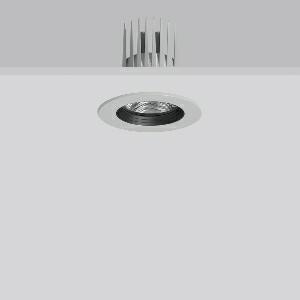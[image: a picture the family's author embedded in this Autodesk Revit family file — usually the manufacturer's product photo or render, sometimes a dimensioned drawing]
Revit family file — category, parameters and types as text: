
# Revit family: heledon_mini_e_901740_004_1_98e3
name_source: partatom
category: Lighting Fixtures
units: mm (PartAtom-declared; Revit-internal decimal feet)

## family parameters
Cut with Voids When Loaded = No
Host = Face
Light Source = No
Part Type = Normal
Room Calculation Point = No
Round Connector Dimension = Use Diameter
Shared = No

## types (1)
- HELEDON mini E (1 x LED Modul 940, 2700 lm, 4000)
    Apparent Load = 20 VA
    Approval mark = CE
    CIE Flux Codes = 100 100 100 100 100
    Color Rendering = 92
    Color Temperature = 4000
    Default Elevation = 1800 mm
    Description = Series: HELEDON mini
Round recessed downlight. Housing: die-cast aluminium, powder-coated. Black plastic ring and recessed LED to prevent glare from the side. Optical assembly with reflector made of MIRO-Silver with 98% total light reflection for outstanding efficiency - can be changed without tools. Best colour rendering index Ra>90. Suitable for Recessed ceiling mounting. Installation without tools thanks to spring fastening system. Including separate LED converter with connecting cable 600 mm.High quality converter without flickering and stroboscopic effect. Through-wiring box (5 pole) available as accessory. The following accessories can be mounted without use of tools: interchangeable lenses, decorative glasses, honeycomb louvre, clear and frosted diffusers, white interchangeable plastic ring. 
Colour: silver
Diameter: 124 mm
Height: 3 mm
Cut-out diameter: 114 mm
Recess height: 170 mm
Luminaire: recess height: 120 mm
Lamp: LED
Socket: without socket
Colour temperature: 4000K
Colour rendering index (CRI): 92
System power: 20 W
Rated luminous flux: 2700 lm
Luminous efficiency: 135 lm/W
Control gear: Regulated power supply
Protection class: II
Type of protection: IP 20
    Height = 0 mm  [stored 0 ft]
    Lamp = 1 x LED Modul 940
    Lamp Light Flux = 2700 lm
    Lamp count = 1
    Length = 124 mm  [stored 0.406824 ft]
    Lifetime = 50000 h
    Luminous efficacy = 135 lm/W
    Manufacturer = RZB
    ModVariant = No
    Model = 901740.004.1
    Mounting Place = Ceiling
    Mounting Type = Recessed
    Number of Poles = 1
    OnlyDefault = Yes
    Power Factor = 1
    Product Name = HELEDON mini E
    Product group = Recessed downlights
    ProductGroupID = 402
    Protection Class = Protection class II
    Protection Degree = IP 20
    RLX_Detail_Level = 1
    RLX_Emergency_Light_Flux = 0 lm
    RLX_Emergency_Type = 0
    RLX_Emergency_Type_DB = No
    RlxData = <blob elided: 127829 chars, md5=203a31c9>
    Socket = socket
    Standby Power = 0 W
    System Light Flux = 2700 lm
    System Power = 20 W
    Type Comments = Product without accessories
    Type Image = 901657.004.jpg
    URL = http://relux.com
    VarID = ---
    Voltage = 230 V
    Voltage Range = 220-240 V
    Weight = 0.00 kg
    Width = 0 mm  [stored 0 ft]

note: [stored X ft] marks values corroborated as IEEE doubles in the binary element streams (Revit-internal decimal feet)

## geometry (parser evidence)
native form markers: Blend x4, Sweep x11
no freeform markers — native parametric forms only
